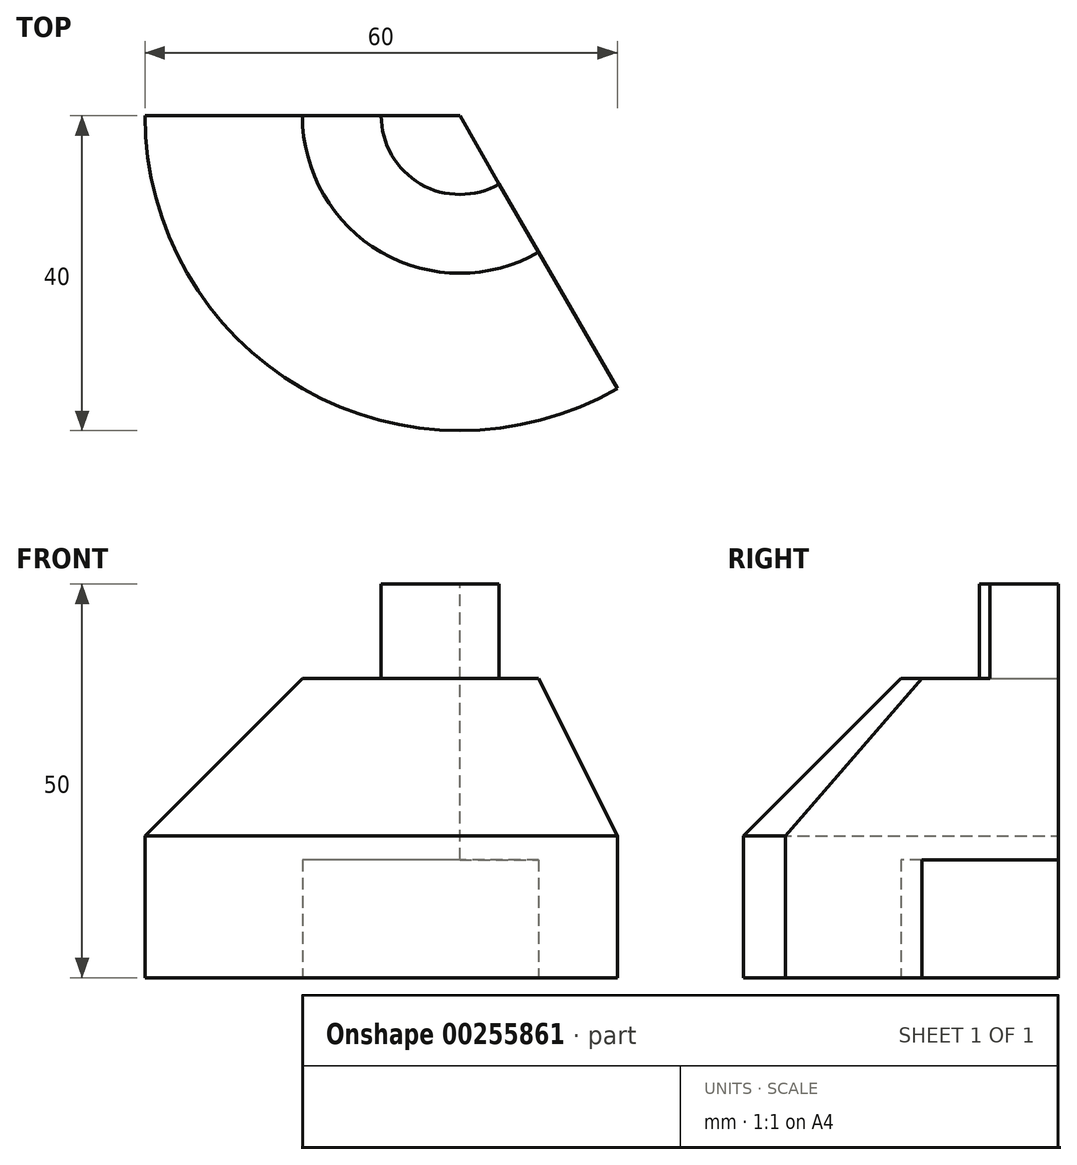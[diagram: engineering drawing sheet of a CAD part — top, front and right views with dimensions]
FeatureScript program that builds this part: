
annotation { "Feature Type Name" : "Feature", "Feature Type Description" : "" }
export const myFeature = defineFeature(function(context is Context, id is Id, definition is map)
    precondition{}
    {
        {
            var Q0;
            Q0=qCreatedBy(makeId("Front.planeOp"),FACE);
            var sketch = newSketch(context, id + "F0", { "sketchPlane" : qUnion([Q0])});
            skLineSegment(sketch, "E0", {"start": v(0, 0) * mm, "end": v(0, 50) * mm});
            skLineSegment(sketch, "E1", {"start": v(0, 50) * mm, "end": v(-10, 50) * mm});
            skLineSegment(sketch, "E2", {"start": v(-10, 50) * mm, "end": v(-10, 38) * mm});
            skLineSegment(sketch, "E3", {"start": v(-10, 38) * mm, "end": v(-20, 38) * mm});
            skLineSegment(sketch, "E4", {"start": v(-20, 38) * mm, "end": v(-40, 18) * mm});
            skLineSegment(sketch, "E5", {"start": v(-40, 18) * mm, "end": v(-40, 0) * mm});
            skLineSegment(sketch, "E6", {"start": v(-40, 0) * mm, "end": v(-20, 0) * mm});
            skLineSegment(sketch, "E7", {"start": v(0, 15) * mm, "end": v(-20, 15) * mm});
            skLineSegment(sketch, "E8", {"start": v(-20, 15) * mm, "end": v(-20, 0) * mm});
            skSolve(sketch);
        }
        {
            var Q0;
            {var subQ0=sQuery(id+"F0.wireOp",EDGE,"E1");Q0=makeQuery(id+"F0.imprint","IMPRINT",FACE,{"disambiguationData":[TD([[makeQuery(id+"F0.imprint","IMPRINT",EDGE,{"derivedFrom":subQ0}),1.0]])]});}
            var Q1;
            Q1=sQuery(id+"F0.wireOp",EDGE,"E0");
            revolve(context, id + "F1", {"entities" : qUnion([Q0]), "axis" : qUnion([Q1]), "revolveType" : RevolveType.ONE_DIRECTION, "angle" : 120 * degree});
        }
    });
